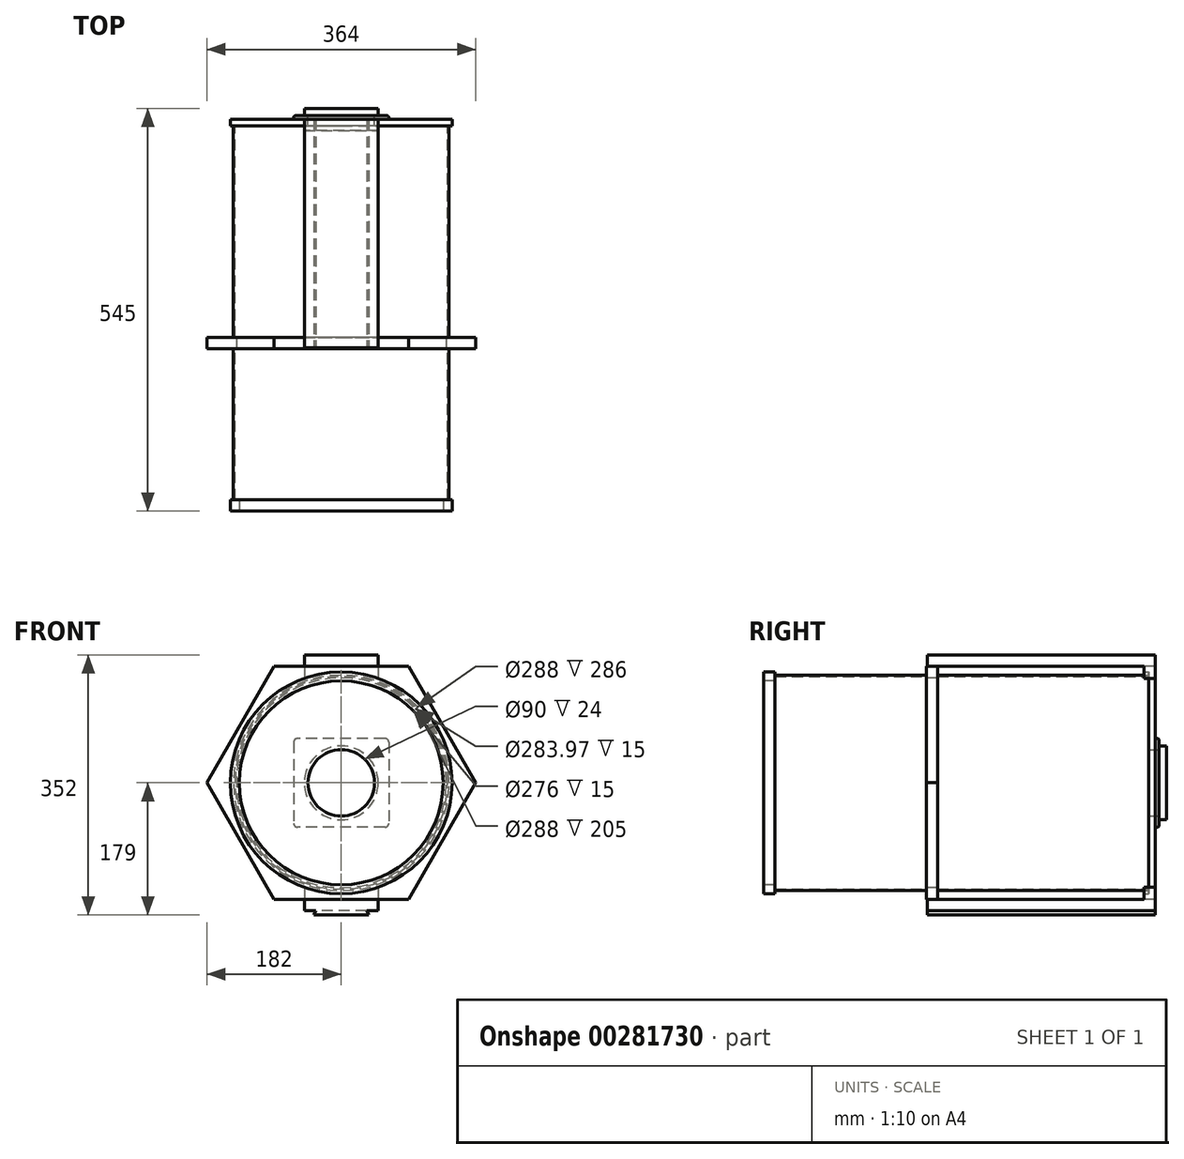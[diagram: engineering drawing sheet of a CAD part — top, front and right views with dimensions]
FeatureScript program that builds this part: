
annotation { "Feature Type Name" : "Feature", "Feature Type Description" : "" }
export const myFeature = defineFeature(function(context is Context, id is Id, definition is map)
    precondition{}
    {
        {
            var Q0;
            Q0=qCreatedBy(makeId("Front.planeOp"),FACE);
            var sketch = newSketch(context, id + "F0", { "sketchPlane" : qUnion([Q0])});
            skCircle(sketch, "E0", {"center": v(0, 0) * mm, "radius": 150 * mm});
            skCircle(sketch, "E1", {"center": v(0, 0) * mm, "radius": 146 * mm});
            skCircle(sketch, "E2", {"center": v(0, 0) * mm, "radius": 144 * mm});
            skLineSegment(sketch, "E3", {"start": v(50, 158) * mm, "end": v(50, 135.04) * mm});
            skLineSegment(sketch, "E4", {"start": v(-50, 158) * mm, "end": v(-50, 135.04) * mm});
            skLineSegment(sketch, "E5", {"start": v(50, 158) * mm, "end": v(-50, 158) * mm});
            skLineSegment(sketch, "E6", {"start": v(50, -158) * mm, "end": v(-50, -158) * mm});
            skLineSegment(sketch, "E7.trimOffspring", {"start": v(50, -135.04) * mm, "end": v(50, -158) * mm});
            skLineSegment(sketch, "E8.trimOffspring", {"start": v(-50, -135.04) * mm, "end": v(-50, -158) * mm});
            skLineSegment(sketch, "E9", {"start": v(0, 0) * mm, "end": v(0, -300.37) * mm, "construction": true});
            skLineSegment(sketch, "E10", {"start": v(34.5, -158) * mm, "end": v(37, -164) * mm});
            skLineSegment(sketch, "E11", {"start": v(37, -164) * mm, "end": v(-37, -164) * mm});
            skLineSegment(sketch, "E12", {"start": v(-37, -164) * mm, "end": v(-34.5, -158) * mm});
            skCircle(sketch, "E13", {"center": v(0, 0) * mm, "radius": 50 * mm});
            skLineSegment(sketch, "E14.bottom", {"start": v(59.33, 60) * mm, "end": v(-59.33, 60) * mm});
            skLineSegment(sketch, "E14.top", {"start": v(59.33, -60) * mm, "end": v(-59.33, -60) * mm});
            skLineSegment(sketch, "E14.left", {"start": v(64.33, 55) * mm, "end": v(64.33, -55) * mm});
            skLineSegment(sketch, "E14.right", {"start": v(-64.33, 55) * mm, "end": v(-64.33, -55) * mm});
            skCircle(sketch, "E15", {"center": v(0, 0) * mm, "radius": 45 * mm});
            skPoint(sketch, "E16.visualSharp", {"position": v(64.33, 60) * mm});
            skArc(sketch, "E16.filletArc", {"start": v(64.33, 55) * mm, "mid": v(62.86, 58.54) * mm, "end": v(59.33, 60) * mm});
            skPoint(sketch, "E17.visualSharp", {"position": v(-64.33, 60) * mm});
            skArc(sketch, "E17.filletArc", {"start": v(-59.33, 60) * mm, "mid": v(-62.86, 58.54) * mm, "end": v(-64.33, 55) * mm});
            skPoint(sketch, "E18.visualSharp", {"position": v(-64.33, -60) * mm});
            skArc(sketch, "E18.filletArc", {"start": v(-64.33, -55) * mm, "mid": v(-62.86, -58.54) * mm, "end": v(-59.33, -60) * mm});
            skPoint(sketch, "E19.visualSharp", {"position": v(64.33, -60) * mm});
            skArc(sketch, "E19.filletArc", {"start": v(59.33, -60) * mm, "mid": v(62.86, -58.54) * mm, "end": v(64.33, -55) * mm});
            skSolve(sketch);
        }
        {
            var Q0;
            Q0=makeQuery(id+"F0.imprint","IMPRINT",FACE,{"disambiguationData":[TD([[makeQuery(id+"F0.imprint","IMPRINT",EDGE,{"derivedFrom":sQuery(id+"F0.wireOp",EDGE,"E1")}),1.0]])]});
            var Q1;
            Q1=sQuery(id+"F0.wireOp",EDGE,"E2");
            var Q2;
            Q2=sQuery(id+"F0.wireOp",EDGE,"E1");
            extrude(context, id + "F1", {"entities" : qUnion([Q0]), "surfaceEntities" : qUnion([Q1, Q2]), "depth" : 530 * mm, "offsetDistance" : 25 * mm});
        }
        {
            var Q0;
            Q0=makeQuery(id+"F0.imprint","IMPRINT",FACE,{"disambiguationData":[TD([[makeQuery(id+"F0.imprint","IMPRINT",EDGE,{"derivedFrom":sQuery(id+"F0.wireOp",EDGE,"E2")}),1.0]])]});
            var Q1;
            Q1=makeQuery(id+"F0.imprint","IMPRINT",FACE,{"disambiguationData":[TD([[makeQuery(id+"F0.imprint","IMPRINT",EDGE,{"derivedFrom":sQuery(id+"F0.wireOp",EDGE,"E0")}),1.0]])]});
            var Q2;
            Q2=makeQuery(id+"F0.imprint","IMPRINT",FACE,{"disambiguationData":[TD([[makeQuery(id+"F0.imprint","IMPRINT",EDGE,{"derivedFrom":sQuery(id+"F0.wireOp",EDGE,"E13")}),-1.0]])]});
            var Q3;
            Q3=makeQuery(id+"F0.imprint","IMPRINT",FACE,{"disambiguationData":[TD([[makeQuery(id+"F0.imprint","IMPRINT",EDGE,{"derivedFrom":sQuery(id+"F0.wireOp",EDGE,"E13")}),1.0]])]});
            extrude(context, id + "F2", {"entities" : qUnion([Q0, Q1, Q2, Q3]), "operationType" : NewBodyOperationType.ADD, "depth" : 9 * mm, "offsetDistance" : 25 * mm});
        }
        {
            var Q0;
            Q0=makeQuery(id+"F1.opExtrude","CAP_FACE",FACE,{"disambiguationData":[OSD([sQuery(id+"F0.wireOp",EDGE,"E1"),sQuery(id+"F0.wireOp",EDGE,"E2")])],"isStart":false});
            var sketch = newSketch(context, id + "F3", { "sketchPlane" : qUnion([Q0])});
            skCircle(sketch, "E20", {"center": v(0, 0) * mm, "radius": 138 * mm});
            skCircle(sketch, "E21", {"center": v(0, 0) * mm, "radius": 150.09 * mm});
            skSolve(sketch);
        }
        {
            var Q0;
            Q0=makeQuery(id+"F3.imprint","IMPRINT",FACE,{"disambiguationData":[TD([[makeQuery(id+"F3.imprint","IMPRINT",EDGE,{"derivedFrom":makeQuery(id+"F1.opExtrude","CAP_EDGE",EDGE,{"disambiguationData":[OSD([sQuery(id+"F0.wireOp",EDGE,"E1")])],"isStart":false})}),1.0]])]});
            var Q1;
            Q1=makeQuery(id+"F3.imprint","IMPRINT",FACE,{"disambiguationData":[TD([[makeQuery(id+"F3.imprint","IMPRINT",EDGE,{"derivedFrom":sQuery(id+"F3.wireOp",EDGE,"E20")}),-1.0]])]});
            var Q2;
            Q2=makeQuery(id+"F3.imprint","IMPRINT",FACE,{"disambiguationData":[TD([[makeQuery(id+"F3.imprint","IMPRINT",EDGE,{"derivedFrom":sQuery(id+"F3.wireOp",EDGE,"E21")}),1.0]])]});
            extrude(context, id + "F4", {"entities" : qUnion([Q0, Q1, Q2]), "operationType" : NewBodyOperationType.ADD, "oppositeDirection" : true, "depth" : 15 * mm, "offsetDistance" : 25 * mm});
        }
        {
            var Q0;
            {var subQ5=sQuery(id+"F0.wireOp",EDGE,"E5");Q0=makeQuery(id+"F0.imprint","IMPRINT",FACE,{"disambiguationData":[TD([[makeQuery(id+"F0.imprint","IMPRINT",EDGE,{"derivedFrom":subQ5}),1.0]])]});}
            var Q1;
            {var subQ5=sQuery(id+"F0.wireOp",EDGE,"E6");Q1=makeQuery(id+"F0.imprint","IMPRINT",FACE,{"disambiguationData":[TD([[makeQuery(id+"F0.imprint","IMPRINT",EDGE,{"derivedFrom":subQ5}),-1.0]])]});}
            extrude(context, id + "F5", {"entities" : qUnion([Q0, Q1]), "operationType" : NewBodyOperationType.ADD, "depth" : 15 * mm, "offsetDistance" : 25 * mm});
        }
        {
            var Q0;
            {var subQ0=sQuery(id+"F0.wireOp",EDGE,"E2");var subQ1=makeQuery(id+"F0.imprint","INTERSECT",VERTEX,{"derivedFrom":[subQ0,sQuery(id+"F0.wireOp",EDGE,"E3")]});Q0=makeQuery(id+"F0.imprint","IMPRINT",FACE,{"disambiguationData":[TD([[makeQuery(id+"F0.imprint","IMPRINT",EDGE,{"disambiguationData":[TD([[subQ1,-1.0]])],"derivedFrom":subQ0}),1.0]])]});}
            cPlane(context, id + "F6", {"entities" : qUnion([Q0]), "cplaneType" : CPlaneType.OFFSET, "offset" : 310 * mm, "width" : 150 * mm, "height" : 150 * mm});
        }
        {
            var Q0;
            Q0=qCreatedBy(id+"F6.planeOp",FACE);
            var sketch = newSketch(context, id + "F7", { "sketchPlane" : qUnion([Q0])});
            skCircle(sketch, "E22.cCircle", {"center": v(0, 0) * mm, "radius": 182 * mm, "construction": true});
            skLineSegment(sketch, "E22.0", {"start": v(-182, 0) * mm, "end": v(-91, 157.62) * mm});
            skLineSegment(sketch, "E22.1", {"start": v(-91, 157.62) * mm, "end": v(91, 157.62) * mm});
            skLineSegment(sketch, "E22.2", {"start": v(91, 157.62) * mm, "end": v(182, 0) * mm});
            skLineSegment(sketch, "E22.3", {"start": v(182, 0) * mm, "end": v(91, -157.62) * mm});
            skLineSegment(sketch, "E22.4", {"start": v(91, -157.62) * mm, "end": v(-91, -157.62) * mm});
            skLineSegment(sketch, "E22.5", {"start": v(-91, -157.62) * mm, "end": v(-182, 0) * mm});
            skCircle(sketch, "E23", {"center": v(0, 0) * mm, "radius": 141.98 * mm});
            skSolve(sketch);
        }
        {
            var Q0;
            Q0=makeQuery(id+"F7.imprint","IMPRINT",FACE,{"disambiguationData":[TD([[makeQuery(id+"F7.imprint","IMPRINT",EDGE,{"derivedFrom":sQuery(id+"F7.wireOp",EDGE,"E22.0")}),-1.0]])]});
            extrude(context, id + "F8", {"entities" : qUnion([Q0]), "operationType" : NewBodyOperationType.ADD, "oppositeDirection" : true, "depth" : 15 * mm, "offsetDistance" : 25 * mm});
        }
        {
            var Q0;
            Q0=makeQuery(id+"F5.opExtrude","SWEPT_FACE",FACE,{"disambiguationData":[OSD([sQuery(id+"F0.wireOp",EDGE,"E5")])]});
            var sketch = newSketch(context, id + "F9", { "sketchPlane" : qUnion([Q0])});
            skLineSegment(sketch, "E24.bottom", {"start": v(50, 0) * mm, "end": v(-49.97, 0) * mm});
            skLineSegment(sketch, "E24.top", {"start": v(50, -308.95) * mm, "end": v(-49.97, -308.95) * mm});
            skLineSegment(sketch, "E24.left", {"start": v(50, 0) * mm, "end": v(50, -308.95) * mm});
            skLineSegment(sketch, "E24.right", {"start": v(-49.97, 0) * mm, "end": v(-49.97, -308.95) * mm});
            skSolve(sketch);
        }
        {
            var Q0;
            {var subQ0=sQuery(id+"F9.wireOp",EDGE,"E24.top");Q0=makeQuery(id+"F9.imprint","IMPRINT",FACE,{"disambiguationData":[TD([[makeQuery(id+"F9.imprint","IMPRINT",EDGE,{"derivedFrom":subQ0}),-1.0]])]});}
            var Q1;
            {var subQ0=sQuery(id+"F9.wireOp",EDGE,"E24.bottom");Q1=makeQuery(id+"F9.imprint","IMPRINT",FACE,{"disambiguationData":[TD([[makeQuery(id+"F9.imprint","IMPRINT",EDGE,{"derivedFrom":subQ0}),1.0]])]});}
            extrude(context, id + "F10", {"entities" : qUnion([Q0, Q1]), "operationType" : NewBodyOperationType.ADD, "depth" : 15 * mm, "offsetDistance" : 25 * mm});
        }
        {
            var Q0;
            Q0=makeQuery(id+"F5.opExtrude","SWEPT_FACE",FACE,{"disambiguationData":[OSD([sQuery(id+"F0.wireOp",EDGE,"E6")])]});
            var sketch = newSketch(context, id + "F11", { "sketchPlane" : qUnion([Q0])});
            skLineSegment(sketch, "E25.bottom", {"start": v(50, 0) * mm, "end": v(-49.97, 0) * mm});
            skLineSegment(sketch, "E25.top", {"start": v(50, 308.83) * mm, "end": v(-49.97, 308.83) * mm});
            skLineSegment(sketch, "E25.left", {"start": v(50, 0) * mm, "end": v(50, 308.83) * mm});
            skLineSegment(sketch, "E25.right", {"start": v(-49.97, 0) * mm, "end": v(-49.97, 308.83) * mm});
            skSolve(sketch);
        }
        {
            var Q0;
            Q0 = qSketchRegion(id + "F11", true);
            extrude(context, id + "F12", {"entities" : qUnion([Q0]), "operationType" : NewBodyOperationType.ADD, "depth" : 15 * mm, "offsetDistance" : 25 * mm});
        }
        {
            var Q0;
            Q0=makeQuery(id+"F12.opExtrude","SWEPT_FACE",FACE,{"disambiguationData":[OSD([sQuery(id+"F11.wireOp",EDGE,"E25.top")])]});
            var sketch = newSketch(context, id + "F13", { "sketchPlane" : qUnion([Q0])});
            skLineSegment(sketch, "E26", {"start": v(34.5, -173) * mm, "end": v(37, -179) * mm});
            skLineSegment(sketch, "E27", {"start": v(37, -179) * mm, "end": v(-37, -179) * mm});
            skLineSegment(sketch, "E28", {"start": v(-37, -179) * mm, "end": v(-34.5, -173) * mm});
            skSolve(sketch);
        }
        {
            var Q0;
            Q0 = qSketchRegion(id + "F13", true);
            var Q1;
            {var subQ0=sQuery(id+"F13.wireOp",EDGE,"E26");Q1=makeQuery(id+"F13.imprint","IMPRINT",FACE,{"disambiguationData":[TD([[makeQuery(id+"F13.imprint","IMPRINT",EDGE,{"derivedFrom":subQ0}),-1.0]])]});}
            extrude(context, id + "F14", {"entities" : qUnion([Q0, Q1]), "operationType" : NewBodyOperationType.ADD, "oppositeDirection" : true, "depth" : 309 * mm, "offsetDistance" : 25 * mm});
        }
        {
            var Q0;
            Q0=makeQuery(id+"F0.imprint","IMPRINT",FACE,{"disambiguationData":[TD([[makeQuery(id+"F0.imprint","IMPRINT",EDGE,{"derivedFrom":sQuery(id+"F0.wireOp",EDGE,"E13")}),1.0]])]});
            extrude(context, id + "F15", {"entities" : qUnion([Q0]), "operationType" : NewBodyOperationType.ADD, "oppositeDirection" : true, "depth" : 15 * mm, "offsetDistance" : 25 * mm});
        }
        {
            var Q0;
            Q0=makeQuery(id+"F0.imprint","IMPRINT",FACE,{"disambiguationData":[TD([[makeQuery(id+"F0.imprint","IMPRINT",EDGE,{"derivedFrom":sQuery(id+"F0.wireOp",EDGE,"E13")}),-1.0]])]});
            extrude(context, id + "F16", {"entities" : qUnion([Q0]), "operationType" : NewBodyOperationType.ADD, "oppositeDirection" : true, "depth" : 5 * mm, "offsetDistance" : 25 * mm});
        }
        {
            var Q0;
            Q0=makeQuery(id+"F16.opExtrude","CAP_EDGE",EDGE,{"disambiguationData":[OSD([sQuery(id+"F0.wireOp",EDGE,"E14.left")])],"isStart":false});
            var Q1;
            Q1=makeQuery(id+"F16.opExtrude","CAP_EDGE",EDGE,{"disambiguationData":[OSD([sQuery(id+"F0.wireOp",EDGE,"E14.bottom")])],"isStart":false});
            var Q2;
            Q2=makeQuery(id+"F16.opExtrude","CAP_EDGE",EDGE,{"disambiguationData":[OSD([sQuery(id+"F0.wireOp",EDGE,"E14.right")])],"isStart":false});
            var Q3;
            Q3=makeQuery(id+"F16.opExtrude","CAP_EDGE",EDGE,{"disambiguationData":[OSD([sQuery(id+"F0.wireOp",EDGE,"E14.top")])],"isStart":false});
            var Q4;
            Q4=makeQuery(id+"F16.opExtrude","CAP_EDGE",EDGE,{"disambiguationData":[OSD([sQuery(id+"F0.wireOp",EDGE,"E13")])],"isStart":false});
            fillet(context, id + "F17", {"entities" : qUnion([Q0, Q1, Q2, Q3, Q4]), "radius" : 2 * mm, "tangentPropagation" : true, "allowEdgeOverflow" : false});
        }
    });
